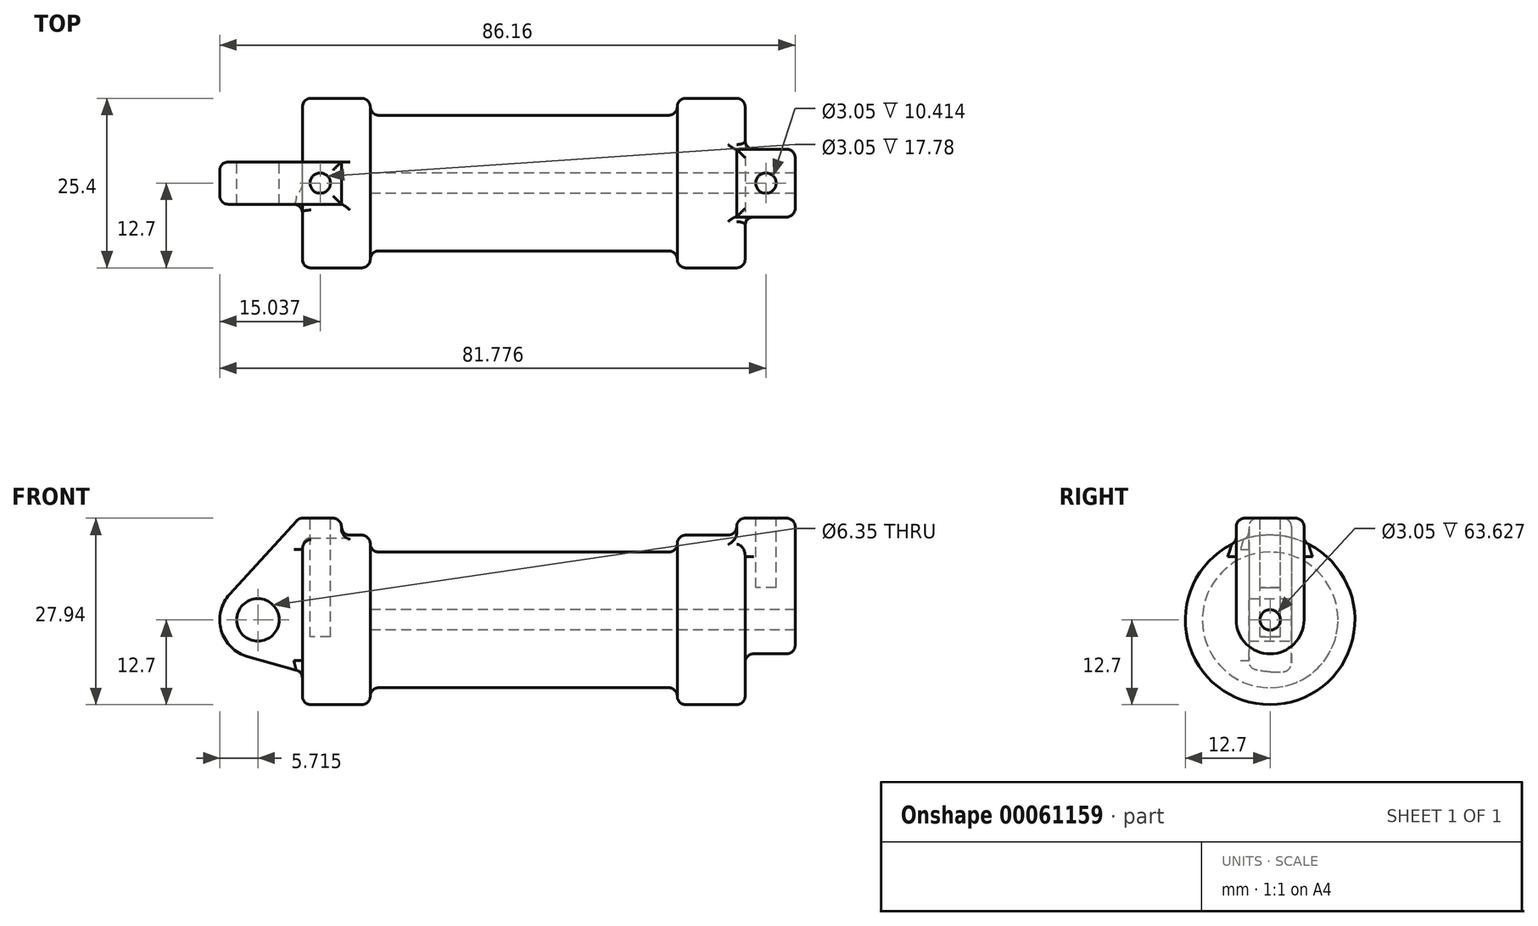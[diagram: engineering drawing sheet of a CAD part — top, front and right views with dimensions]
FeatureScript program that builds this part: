
annotation { "Feature Type Name" : "Feature", "Feature Type Description" : "" }
export const myFeature = defineFeature(function(context is Context, id is Id, definition is map)
    precondition{}
    {
        {
            var Q0;
            Q0=qCreatedBy(makeId("Front.planeOp"),FACE);
            var sketch = newSketch(context, id + "F0", { "sketchPlane" : qUnion([Q0])});
            skLineSegment(sketch, "E0", {"start": v(0, 0) * mm, "end": v(0, 12.7) * mm});
            skLineSegment(sketch, "E1", {"start": v(0, 12.7) * mm, "end": v(10.16, 12.7) * mm});
            skLineSegment(sketch, "E2", {"start": v(10.16, 12.7) * mm, "end": v(10.16, 10.16) * mm});
            skLineSegment(sketch, "E3", {"start": v(10.16, 10.16) * mm, "end": v(56.13, 10.16) * mm});
            skLineSegment(sketch, "E4", {"start": v(56.13, 10.16) * mm, "end": v(56.13, 12.7) * mm});
            skLineSegment(sketch, "E5", {"start": v(56.13, 12.7) * mm, "end": v(66.3, 12.7) * mm});
            skLineSegment(sketch, "E6", {"start": v(66.3, 12.7) * mm, "end": v(66.3, 0) * mm});
            skLineSegment(sketch, "E7", {"start": v(66.3, 0) * mm, "end": v(0, 0) * mm});
            skLineSegment(sketch, "E8", {"start": v(5.84, 15.24) * mm, "end": v(-0.5, 15.24) * mm});
            skLineSegment(sketch, "E9", {"start": v(-0.5, 15.24) * mm, "end": v(-10.88, 3.85) * mm});
            skLineSegment(sketch, "E10", {"start": v(0, 0) * mm, "end": v(-6.65, 0) * mm});
            skCircle(sketch, "E11", {"center": v(-6.65, 0) * mm, "radius": 5.72 * mm});
            skCircle(sketch, "E12", {"center": v(-6.65, 0) * mm, "radius": 3.18 * mm});
            skLineSegment(sketch, "E13", {"start": v(5.84, 15.24) * mm, "end": v(5.84, -9.4) * mm});
            skLineSegment(sketch, "E14", {"start": v(5.84, -9.4) * mm, "end": v(-8.18, -5.5) * mm});
            skSolve(sketch);
        }
        {
            var Q0;
            {var subQ0=sQuery(id+"F0.wireOp",EDGE,"E2");Q0=makeQuery(id+"F0.imprint","IMPRINT",FACE,{"disambiguationData":[TD([[makeQuery(id+"F0.imprint","IMPRINT",EDGE,{"derivedFrom":subQ0}),-1.0]])]});}
            var Q1;
            {var subQ0=sQuery(id+"F0.wireOp",EDGE,"E0");Q1=makeQuery(id+"F0.imprint","IMPRINT",FACE,{"disambiguationData":[TD([[makeQuery(id+"F0.imprint","IMPRINT",EDGE,{"derivedFrom":subQ0}),-1.0]])]});}
            var Q2;
            Q2=sQuery(id+"F0.wireOp",EDGE,"E7");
            revolve(context, id + "F1", {"entities" : qUnion([Q0, Q1]), "axis" : qUnion([Q2]), "revolveType" : RevolveType.FULL});
        }
        {
            var Q0;
            {var subQ3=sQuery(id+"F0.wireOp",EDGE,"E0");Q0=makeQuery(id+"F0.imprint","IMPRINT",FACE,{"disambiguationData":[TD([[makeQuery(id+"F0.imprint","IMPRINT",EDGE,{"derivedFrom":subQ3}),1.0]])]});}
            var Q1;
            {var subQ4=sQuery(id+"F0.wireOp",EDGE,"E12");Q1=makeQuery(id+"F0.imprint","IMPRINT",FACE,{"disambiguationData":[TD([[makeQuery(id+"F0.imprint","IMPRINT",EDGE,{"derivedFrom":subQ4}),-1.0]])]});}
            var Q2;
            {var subQ0=sQuery(id+"F0.wireOp",EDGE,"E14");Q2=makeQuery(id+"F0.imprint","IMPRINT",FACE,{"disambiguationData":[TD([[makeQuery(id+"F0.imprint","IMPRINT",EDGE,{"derivedFrom":subQ0}),-1.0]])]});}
            var Q3;
            {var subQ0=sQuery(id+"F0.wireOp",EDGE,"E0");Q3=makeQuery(id+"F0.imprint","IMPRINT",FACE,{"disambiguationData":[TD([[makeQuery(id+"F0.imprint","IMPRINT",EDGE,{"derivedFrom":subQ0}),-1.0]])]});}
            extrude(context, id + "F2", {"entities" : qUnion([Q0, Q1, Q2, Q3]), "operationType" : NewBodyOperationType.ADD, "endBound" : BoundingType.SYMMETRIC, "depth" : 6.35 * mm});
        }
        {
            var Q0;
            Q0=makeQuery(id+"F1.opRevolve","SWEPT_FACE",FACE,{"disambiguationData":[OSD([sQuery(id+"F0.wireOp",EDGE,"E6")])]});
            var sketch = newSketch(context, id + "F3", { "sketchPlane" : qUnion([Q0])});
            skCircle(sketch, "E15", {"center": v(0, 0) * mm, "radius": 5.08 * mm});
            skCircle(sketch, "E16", {"center": v(0, 0) * mm, "radius": 1.52 * mm});
            skLineSegment(sketch, "E17", {"start": v(-5.08, 0) * mm, "end": v(-5.08, 15.24) * mm});
            skLineSegment(sketch, "E18", {"start": v(5.08, 0) * mm, "end": v(5.08, 15.24) * mm});
            skLineSegment(sketch, "E19", {"start": v(5.08, 15.24) * mm, "end": v(-5.08, 15.24) * mm});
            skSolve(sketch);
        }
        {
            var Q0;
            {var subQ0=sQuery(id+"F3.wireOp",EDGE,"E19");Q0=makeQuery(id+"F3.imprint","IMPRINT",FACE,{"disambiguationData":[TD([[makeQuery(id+"F3.imprint","IMPRINT",EDGE,{"derivedFrom":subQ0}),1.0]])]});}
            var Q1;
            {var subQ0=sQuery(id+"F3.wireOp",EDGE,"E17");var subQ1=sQuery(id+"F3.wireOp",EDGE,"E15");var subQ2=makeQuery(id+"F3.imprint","INTERSECT",VERTEX,{"derivedFrom":[subQ1,subQ0]});Q1=makeQuery(id+"F3.imprint","IMPRINT",FACE,{"disambiguationData":[TD([[makeQuery(id+"F3.imprint","IMPRINT",EDGE,{"disambiguationData":[TD([[subQ2,1.0]])],"derivedFrom":subQ1}),-1.0]])]});}
            var Q2;
            Q2=makeQuery(id+"F3.imprint","IMPRINT",FACE,{"disambiguationData":[TD([[makeQuery(id+"F3.imprint","IMPRINT",EDGE,{"derivedFrom":sQuery(id+"F3.wireOp",EDGE,"E16")}),-1.0]])]});
            extrude(context, id + "F4", {"entities" : qUnion([Q0, Q1, Q2]), "operationType" : NewBodyOperationType.ADD, "oppositeDirection" : true, "depth" : 1.27 * mm});
        }
        {
            var Q0;
            {var subQ0=sQuery(id+"F3.wireOp",EDGE,"E19");Q0=makeQuery(id+"F3.imprint","IMPRINT",FACE,{"disambiguationData":[TD([[makeQuery(id+"F3.imprint","IMPRINT",EDGE,{"derivedFrom":subQ0}),1.0]])]});}
            var Q1;
            {var subQ0=sQuery(id+"F3.wireOp",EDGE,"E17");var subQ1=sQuery(id+"F3.wireOp",EDGE,"E15");var subQ2=makeQuery(id+"F3.imprint","INTERSECT",VERTEX,{"derivedFrom":[subQ1,subQ0]});Q1=makeQuery(id+"F3.imprint","IMPRINT",FACE,{"disambiguationData":[TD([[makeQuery(id+"F3.imprint","IMPRINT",EDGE,{"disambiguationData":[TD([[subQ2,1.0]])],"derivedFrom":subQ1}),-1.0]])]});}
            var Q2;
            Q2=makeQuery(id+"F3.imprint","IMPRINT",FACE,{"disambiguationData":[TD([[makeQuery(id+"F3.imprint","IMPRINT",EDGE,{"derivedFrom":sQuery(id+"F3.wireOp",EDGE,"E16")}),-1.0]])]});
            extrude(context, id + "F5", {"entities" : qUnion([Q0, Q1, Q2]), "operationType" : NewBodyOperationType.ADD, "depth" : 7.5 * mm});
        }
        {
            var Q0;
            Q0=makeQuery(id+"F3.imprint","IMPRINT",FACE,{"disambiguationData":[TD([[makeQuery(id+"F3.imprint","IMPRINT",EDGE,{"derivedFrom":sQuery(id+"F3.wireOp",EDGE,"E16")}),1.0]])]});
            var Q1;
            Q1=makeQuery(id+"F1.opRevolve","SWEPT_FACE",FACE,{"disambiguationData":[OSD([sQuery(id+"F0.wireOp",EDGE,"E2")])]});
            extrude(context, id + "F6", {"entities" : qUnion([Q0]), "operationType" : NewBodyOperationType.REMOVE, "endBound" : BoundingType.UP_TO_SURFACE, "oppositeDirection" : true, "endBoundEntityFace" : qUnion([Q1]), "depth" : 25.4 * mm});
        }
        {
            var Q0;
            Q0=makeQuery(id+"F2.opExtrude","SWEPT_FACE",FACE,{"disambiguationData":[OSD([sQuery(id+"F0.wireOp",EDGE,"E8")])]});
            var sketch = newSketch(context, id + "F7", { "sketchPlane" : qUnion([Q0])});
            skCircle(sketch, "E20", {"center": v(2.67, 0) * mm, "radius": 1.52 * mm});
            skPoint(sketch, "E20.centerSnap0", {"position": v(2.67, -3.18) * mm});
            skPoint(sketch, "E20.centerSnap1", {"position": v(5.84, 0) * mm});
            skSolve(sketch);
        }
        {
            var Q0;
            {var subQ0=sQuery(id+"F3.wireOp",EDGE,"E19");Q0=makeQuery(id+"F5.boolean.opBoolean","MERGE",FACE,{"derivedFrom":[makeQuery(id+"F4.opExtrude","SWEPT_FACE",FACE,{"disambiguationData":[OSD([subQ0])]}),makeQuery(id+"F5.opExtrude","SWEPT_FACE",FACE,{"disambiguationData":[OSD([subQ0])]})]});}
            var sketch = newSketch(context, id + "F8", { "sketchPlane" : qUnion([Q0])});
            skCircle(sketch, "E21", {"center": v(69.4, 0) * mm, "radius": 1.52 * mm});
            skPoint(sketch, "E21.centerSnap0", {"position": v(73.79, 0) * mm});
            skPoint(sketch, "E21.centerSnap1", {"position": v(69.4, -5.08) * mm});
            skSolve(sketch);
        }
        {
            var Q0;
            Q0=makeQuery(id+"F8.imprint","IMPRINT",FACE,{"disambiguationData":[TD([[makeQuery(id+"F8.imprint","IMPRINT",EDGE,{"derivedFrom":sQuery(id+"F8.wireOp",EDGE,"E21")}),1.0]])]});
            var Q1;
            Q1=sQuery(id+"F8.wireOp",EDGE,"E21");
            extrude(context, id + "F9", {"entities" : qUnion([Q0]), "operationType" : NewBodyOperationType.REMOVE, "surfaceEntities" : qUnion([Q1]), "oppositeDirection" : true, "depth" : 10.4 * mm});
        }
        {
            var Q0;
            Q0=makeQuery(id+"F7.imprint","IMPRINT",FACE,{"disambiguationData":[TD([[makeQuery(id+"F7.imprint","IMPRINT",EDGE,{"derivedFrom":sQuery(id+"F7.wireOp",EDGE,"E20")}),1.0]])]});
            var Q1;
            Q1=sQuery(id+"F7.wireOp",EDGE,"E20");
            extrude(context, id + "F10", {"entities" : qUnion([Q0]), "operationType" : NewBodyOperationType.REMOVE, "surfaceEntities" : qUnion([Q1]), "oppositeDirection" : true, "depth" : 17.78 * mm});
        }
        {
            var Q0;
            Q0=makeQuery(id+"F1.opRevolve","SWEPT_EDGE",EDGE,{"disambiguationData":[OSD([sQuery(id+"F0.wireOp",EDGE,"E0"),sQuery(id+"F0.wireOp",EDGE,"E1")])]});
            var Q1;
            Q1=makeQuery(id+"F1.opRevolve","SWEPT_EDGE",EDGE,{"disambiguationData":[OSD([sQuery(id+"F0.wireOp",EDGE,"E1"),sQuery(id+"F0.wireOp",EDGE,"E2")])]});
            var Q2;
            Q2=makeQuery(id+"F1.opRevolve","SWEPT_EDGE",EDGE,{"disambiguationData":[OSD([sQuery(id+"F0.wireOp",EDGE,"E2"),sQuery(id+"F0.wireOp",EDGE,"E3")])]});
            var Q3;
            Q3=makeQuery(id+"F1.opRevolve","SWEPT_EDGE",EDGE,{"disambiguationData":[OSD([sQuery(id+"F0.wireOp",EDGE,"E5"),sQuery(id+"F0.wireOp",EDGE,"E6")])]});
            var Q4;
            Q4=makeQuery(id+"F1.opRevolve","SWEPT_EDGE",EDGE,{"disambiguationData":[OSD([sQuery(id+"F0.wireOp",EDGE,"E4"),sQuery(id+"F0.wireOp",EDGE,"E5")])]});
            var Q5;
            Q5=makeQuery(id+"F1.opRevolve","SWEPT_EDGE",EDGE,{"disambiguationData":[OSD([sQuery(id+"F0.wireOp",EDGE,"E3"),sQuery(id+"F0.wireOp",EDGE,"E4")])]});
            fillet(context, id + "F11", {"entities" : qUnion([Q0, Q1, Q2, Q3, Q4, Q5]), "radius" : 1.27 * mm, "tangentPropagation" : true, "allowEdgeOverflow" : false});
        }
        {
            var Q0;
            Q0=makeQuery(id+"F2.opExtrude","CAP_EDGE",EDGE,{"disambiguationData":[OSD([sQuery(id+"F0.wireOp",EDGE,"E9")])],"isStart":false});
            var Q1;
            Q1=makeQuery(id+"F2.opExtrude","CAP_EDGE",EDGE,{"disambiguationData":[OSD([sQuery(id+"F0.wireOp",EDGE,"E9")])],"isStart":true});
            var Q2;
            Q2=makeQuery(id+"F2.opExtrude","CAP_EDGE",EDGE,{"disambiguationData":[OSD([sQuery(id+"F0.wireOp",EDGE,"E8")])],"isStart":false});
            var Q3;
            Q3=makeQuery(id+"F2.opExtrude","CAP_EDGE",EDGE,{"disambiguationData":[OSD([sQuery(id+"F0.wireOp",EDGE,"E8")])],"isStart":true});
            var Q4;
            Q4=makeQuery(id+"F2.opExtrude","SWEPT_EDGE",EDGE,{"disambiguationData":[OSD([sQuery(id+"F0.wireOp",EDGE,"E8"),sQuery(id+"F0.wireOp",EDGE,"E13")])]});
            var Q5;
            Q5=makeQuery(id+"F2.boolean.opBoolean","INTERSECT",EDGE,{"derivedFrom":[makeQuery(id+"F1.opRevolve","SWEPT_FACE",FACE,{"disambiguationData":[OSD([sQuery(id+"F0.wireOp",EDGE,"E1")])]}),makeQuery(id+"F2.opExtrude","SWEPT_FACE",FACE,{"disambiguationData":[OSD([sQuery(id+"F0.wireOp",EDGE,"E13")])]})]});
            var Q6;
            Q6=makeQuery(id+"F2.boolean.opBoolean","INTERSECT",EDGE,{"derivedFrom":[makeQuery(id+"F1.opRevolve","SWEPT_FACE",FACE,{"disambiguationData":[OSD([sQuery(id+"F0.wireOp",EDGE,"E1")])]}),makeQuery(id+"F2.opExtrude","CAP_FACE",FACE,{"disambiguationData":[OSD([sQuery(id+"F0.wireOp",EDGE,"E8"),sQuery(id+"F0.wireOp",EDGE,"E9"),sQuery(id+"F0.wireOp",EDGE,"E11"),sQuery(id+"F0.wireOp",EDGE,"E12"),sQuery(id+"F0.wireOp",EDGE,"E13"),sQuery(id+"F0.wireOp",EDGE,"E14")])],"isStart":false})]});
            var Q7;
            Q7=makeQuery(id+"F2.opExtrude","SWEPT_EDGE",EDGE,{"disambiguationData":[OSD([sQuery(id+"F0.wireOp",EDGE,"E8"),sQuery(id+"F0.wireOp",EDGE,"E9")])]});
            fillet(context, id + "F12", {"entities" : qUnion([Q0, Q1, Q2, Q3, Q4, Q5, Q6, Q7]), "radius" : 1.27 * mm, "tangentPropagation" : true, "allowEdgeOverflow" : false});
        }
        {
            var Q0;
            Q0=makeQuery(id+"F5.opExtrude","CAP_EDGE",EDGE,{"disambiguationData":[OSD([sQuery(id+"F3.wireOp",EDGE,"E18")])],"isStart":false});
            var Q1;
            Q1=makeQuery(id+"F5.opExtrude","CAP_EDGE",EDGE,{"disambiguationData":[OSD([sQuery(id+"F3.wireOp",EDGE,"E18")])],"isStart":true});
            var Q2;
            {var subQ0=sQuery(id+"F3.wireOp",EDGE,"E19");var subQ1=sQuery(id+"F3.wireOp",EDGE,"E18");Q2=makeQuery(id+"F5.boolean.opBoolean","MERGE",EDGE,{"derivedFrom":[makeQuery(id+"F4.opExtrude","SWEPT_EDGE",EDGE,{"disambiguationData":[OSD([subQ1,subQ0])]}),makeQuery(id+"F5.opExtrude","SWEPT_EDGE",EDGE,{"disambiguationData":[OSD([subQ1,subQ0])]})]});}
            var Q3;
            Q3=makeQuery(id+"F5.opExtrude","CAP_EDGE",EDGE,{"disambiguationData":[OSD([sQuery(id+"F3.wireOp",EDGE,"E19")])],"isStart":false});
            var Q4;
            {var subQ0=sQuery(id+"F3.wireOp",EDGE,"E19");var subQ1=sQuery(id+"F3.wireOp",EDGE,"E17");Q4=makeQuery(id+"F5.boolean.opBoolean","MERGE",EDGE,{"derivedFrom":[makeQuery(id+"F4.opExtrude","SWEPT_EDGE",EDGE,{"disambiguationData":[OSD([subQ1,subQ0])]}),makeQuery(id+"F5.opExtrude","SWEPT_EDGE",EDGE,{"disambiguationData":[OSD([subQ1,subQ0])]})]});}
            var Q5;
            Q5=makeQuery(id+"F4.opExtrude","CAP_EDGE",EDGE,{"disambiguationData":[OSD([sQuery(id+"F3.wireOp",EDGE,"E19")])],"isStart":false});
            var Q6;
            Q6=makeQuery(id+"F4.boolean.opBoolean","INTERSECT",EDGE,{"derivedFrom":[makeQuery(id+"F1.opRevolve","SWEPT_FACE",FACE,{"disambiguationData":[OSD([sQuery(id+"F0.wireOp",EDGE,"E5")])]}),makeQuery(id+"F4.opExtrude","CAP_FACE",FACE,{"disambiguationData":[OSD([sQuery(id+"F3.wireOp",EDGE,"E15"),sQuery(id+"F3.wireOp",EDGE,"E16"),sQuery(id+"F3.wireOp",EDGE,"E17"),sQuery(id+"F3.wireOp",EDGE,"E18"),sQuery(id+"F3.wireOp",EDGE,"E19")])],"isStart":false})]});
            fillet(context, id + "F13", {"entities" : qUnion([Q0, Q1, Q2, Q3, Q4, Q5, Q6]), "radius" : 1.27 * mm, "tangentPropagation" : true, "allowEdgeOverflow" : false});
        }
    });
